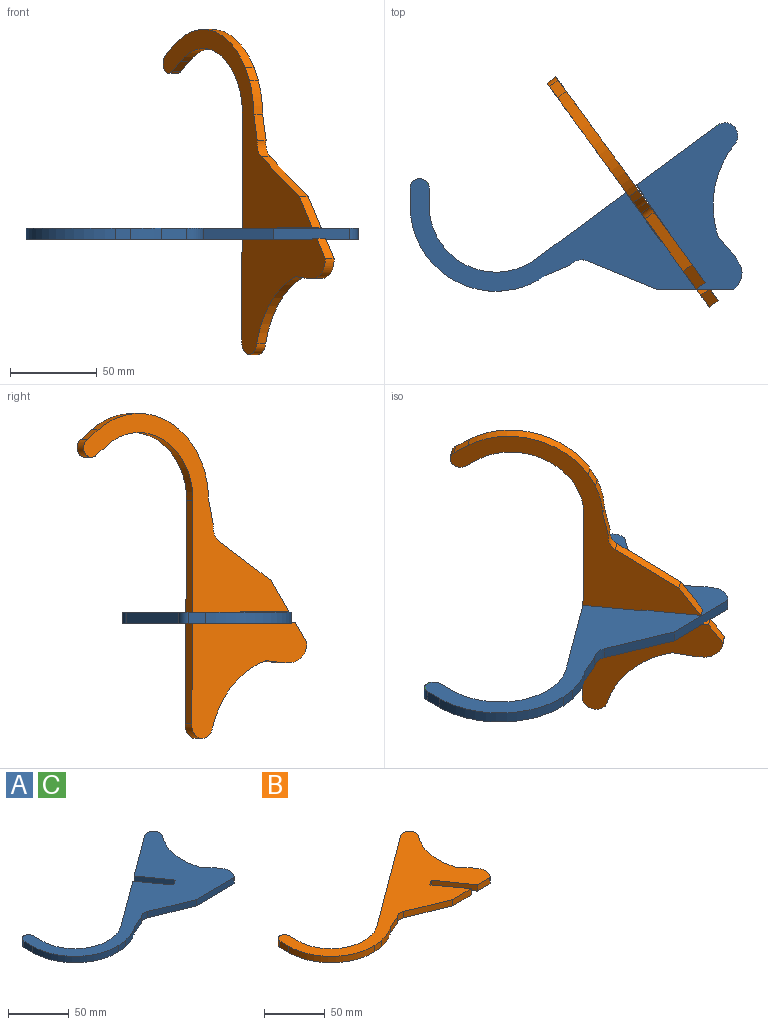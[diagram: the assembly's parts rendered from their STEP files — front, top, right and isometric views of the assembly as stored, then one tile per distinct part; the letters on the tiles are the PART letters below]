
ASSEMBLY  parts=3 mates=1
PART A: 26 faces, bbox 191.4x97.1x6.4 mm
  f0: plane 45.67x33.63mm, normal (-0.59,0.81,0), area 360.2mm2, adj f1,f2,f19,f25
  f1: plane 191.37x97.14mm, normal (0,0,1), area 6572.1mm2, adj f0,f3,f4,f5,f6,f7,f8,f9
  f2: plane 191.37x97.14mm, normal (0,0,-1), area 6572.1mm2, adj f0,f3,f4,f5,f6,f7,f8,f9
  f3: cylinder r=5.5mm len=11.01mm, axis (0,0,-1), area 109.8mm2, adj f1,f2,f4,f22
  f4: plane 9.93x6.35mm, normal (-1,0,0), area 63.1mm2, adj f1,f2,f3,f5
  f5: cylinder r=49.54mm len=51.43mm, axis (0,0,-1), area 506.1mm2, adj f1,f2,f4,f6
  f6: plane 8.74x6.35mm, normal (0.13,-0.99,0), area 56mm2, adj f1,f2,f5,f7
  f7: cylinder r=49.54mm len=17.83mm, axis (0,0,-1), area 124.5mm2, adj f1,f2,f6,f8
  f8: plane 6.35x0mm, normal (0,1,0), area 0mm2, adj f1,f2,f7,f9
  f9: plane 14.41x6.35mm, normal (0.4,-0.92,0), area 99.7mm2, adj f1,f2,f8,f10
  f10: cylinder r=9.13mm len=9.89mm, axis (0,0,-1), area 68.4mm2, adj f1,f2,f9,f11
  f11: plane 40.44x16.64mm, normal (-0.38,-0.92,0), area 277.7mm2, adj f1,f2,f10,f12
  f12: plane 44.01x6.35mm, normal (0.01,-1,0), area 279.4mm2, adj f1,f2,f11,f13
  f13: cylinder r=11.39mm len=16.63mm, axis (0,0,-1), area 119.3mm2, adj f1,f2,f12,f14
  f14: cylinder r=8.94mm len=6.35mm, axis (0,0,-1), area 21.3mm2, adj f1,f2,f13,f15
  f15: plane 10.33x9.09mm, normal (0.75,0.66,0), area 87.4mm2, adj f1,f2,f14,f16
  f16: cylinder r=56.22mm len=53.35mm, axis (0,0,-1), area 358.5mm2, adj f1,f2,f15,f17
  f17: plane 6.35x0.06mm, normal (1,0,0), area 0.4mm2, adj f1,f2,f16,f18
  f18: cylinder r=7.41mm len=12.71mm, axis (0,0,-1), area 147.8mm2, adj f1,f2,f17,f19
  f19: plane 6.35x0.16mm, normal (0,1,0), area 1mm2, adj f0,f1,f2,f18
  f20: plane 51.8x38.15mm, normal (-0.59,0.81,0), area 408.5mm2, adj f1,f2,f21,f23
  f21: cylinder r=38.53mm len=61.5mm, axis (0,0,-1), area 540.6mm2, adj f1,f2,f20,f22
  f22: plane 9.93x6.35mm, normal (1,0,0), area 63.1mm2, adj f1,f2,f3,f21
  f23: plane 27.83x20.22mm, normal (0.81,0.59,0), area 218.4mm2, adj f1,f2,f20,f24
  f24: plane 6.35x5.63mm, normal (-0.59,0.81,0), area 44.2mm2, adj f1,f2,f23,f25
  f25: plane 28.26x19.71mm, normal (-0.82,-0.57,0), area 218.8mm2, adj f0,f1,f2,f24
PART B: 26 faces, bbox 191.4x97.1x6.4 mm
  f0: plane 14.38x6.35mm, normal (0.01,-1,0), area 91.3mm2, adj f1,f2,f13,f25
  f1: plane 191.37x97.14mm, normal (0,0,1), area 6581.2mm2, adj f0,f3,f4,f5,f6,f7,f8,f9
  f2: plane 191.37x97.14mm, normal (0,0,-1), area 6581.2mm2, adj f0,f3,f4,f5,f6,f7,f8,f9
  f3: cylinder r=5.5mm len=11.01mm, axis (0,0,-1), area 109.8mm2, adj f1,f2,f4,f22
  f4: plane 9.93x6.35mm, normal (-1,0,0), area 63.1mm2, adj f1,f2,f3,f5
  f5: cylinder r=49.54mm len=51.43mm, axis (0,0,-1), area 506.1mm2, adj f1,f2,f4,f6
  f6: plane 8.74x6.35mm, normal (0.13,-0.99,0), area 56mm2, adj f1,f2,f5,f7
  f7: cylinder r=49.54mm len=17.83mm, axis (0,0,-1), area 124.5mm2, adj f1,f2,f6,f8
  f8: plane 6.35x0mm, normal (0,1,0), area 0mm2, adj f1,f2,f7,f9
  f9: plane 14.41x6.35mm, normal (0.4,-0.92,0), area 99.7mm2, adj f1,f2,f8,f10
  f10: cylinder r=9.13mm len=9.89mm, axis (0,0,-1), area 68.4mm2, adj f1,f2,f9,f11
  f11: plane 40.44x16.64mm, normal (-0.38,-0.92,0), area 277.7mm2, adj f1,f2,f10,f12
  f12: plane 22x6.35mm, normal (0.01,-1,0), area 139.7mm2, adj f1,f2,f11,f24
  f13: cylinder r=11.39mm len=16.63mm, axis (0,0,-1), area 119.3mm2, adj f0,f1,f2,f14
  f14: cylinder r=8.94mm len=6.35mm, axis (0,0,-1), area 21.3mm2, adj f1,f2,f13,f15
  f15: plane 10.33x9.09mm, normal (0.75,0.66,0), area 87.4mm2, adj f1,f2,f14,f16
  f16: cylinder r=56.22mm len=53.35mm, axis (0,0,-1), area 358.5mm2, adj f1,f2,f15,f17
  f17: plane 6.35x0.06mm, normal (1,0,0), area 0.4mm2, adj f1,f2,f16,f18
  f18: cylinder r=7.41mm len=12.71mm, axis (0,0,-1), area 147.8mm2, adj f1,f2,f17,f19
  f19: plane 6.35x0.16mm, normal (0,1,0), area 1mm2, adj f1,f2,f18,f20
  f20: plane 103.61x76.31mm, normal (-0.59,0.81,0), area 817.1mm2, adj f1,f2,f19,f21
  f21: cylinder r=38.53mm len=61.5mm, axis (0,0,-1), area 540.6mm2, adj f1,f2,f20,f22
  f22: plane 9.93x6.35mm, normal (1,0,0), area 63.1mm2, adj f1,f2,f3,f21
  f23: plane 6.35x5.63mm, normal (0.59,-0.81,0), area 44.2mm2, adj f1,f2,f24,f25
  f24: plane 27.83x20.22mm, normal (0.81,0.59,0), area 218.4mm2, adj f1,f2,f12,f23
  f25: plane 31.85x22.21mm, normal (-0.82,-0.57,0), area 246.5mm2, adj f0,f1,f2,f23
PART C: same geometry as A
PLACE A t=(-7.95,14.73,38.71)mm
PLACE B rot(axis=(-0.59,0.81,0),90deg) t=(3.64,23.15,59.38)mm
PLACE C t=(-7.95,14.73,38.71)mm
MATE fastened B.f23 <-> A.f24  axis (0.59,-0.81,0) through (27.16,-3.84,41.88)mm
